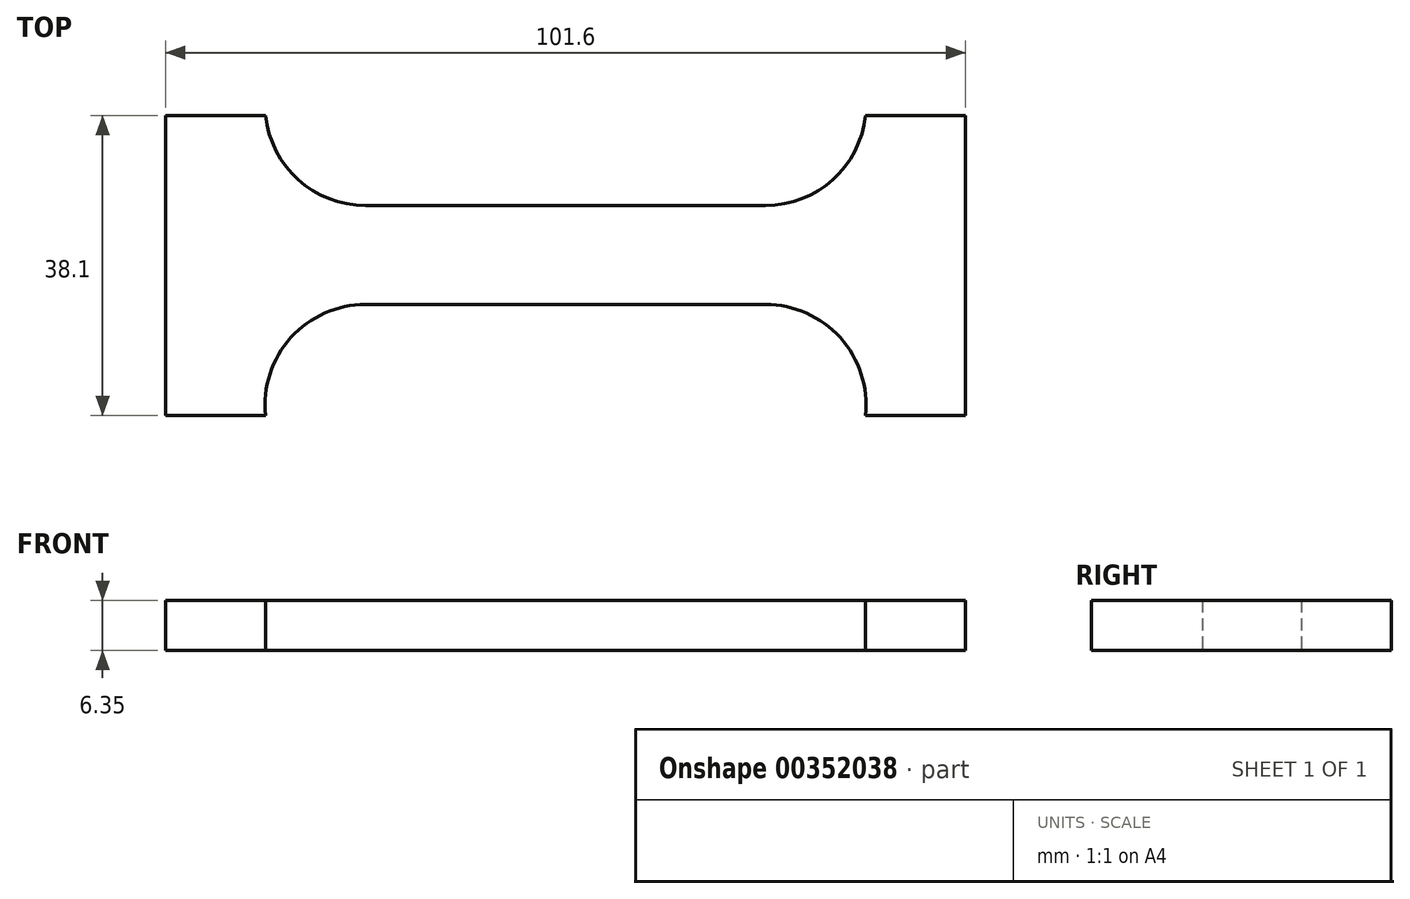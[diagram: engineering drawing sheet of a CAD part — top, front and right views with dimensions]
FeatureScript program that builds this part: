
annotation { "Feature Type Name" : "Feature", "Feature Type Description" : "" }
export const myFeature = defineFeature(function(context is Context, id is Id, definition is map)
    precondition{}
    {
        {
            var Q0;
            Q0=qCreatedBy(makeId("Top.planeOp"),FACE);
            var sketch = newSketch(context, id + "F0", { "sketchPlane" : qUnion([Q0])});
            skLineSegment(sketch, "E0", {"start": v(0, 0) * mm, "end": v(0, 6.28) * mm});
            skLineSegment(sketch, "E1", {"start": v(0, 6.28) * mm, "end": v(25.4, 6.28) * mm});
            skLineSegment(sketch, "E2", {"start": v(38.1, 17.7) * mm, "end": v(50.8, 17.7) * mm});
            skLineSegment(sketch, "E3", {"start": v(50.8, 17.7) * mm, "end": v(50.8, -20.4) * mm});
            skLineSegment(sketch, "E4", {"start": v(50.8, -20.4) * mm, "end": v(38.1, -20.4) * mm});
            skLineSegment(sketch, "E5", {"start": v(25.4, -6.28) * mm, "end": v(0, -6.28) * mm});
            skLineSegment(sketch, "E6", {"start": v(0, -6.28) * mm, "end": v(0, 0) * mm});
            skArc(sketch, "E7", {"start": v(25.4, 6.28) * mm, "mid": v(33.94, 9.56) * mm, "end": v(38.1, 17.7) * mm});
            skArc(sketch, "E8", {"start": v(25.4, -6.28) * mm, "mid": v(34.9, -10.5) * mm, "end": v(38.1, -20.4) * mm});
            skLineSegment(sketch, "E9.MirrorCS", {"start": v(-50.8, -20.4) * mm, "end": v(-38.1, -20.4) * mm});
            skLineSegment(sketch, "E10.MirrorCS", {"start": v(-50.8, 17.7) * mm, "end": v(-50.8, -20.4) * mm});
            skLineSegment(sketch, "E11.MirrorCS", {"start": v(-38.1, 17.7) * mm, "end": v(-50.8, 17.7) * mm});
            skLineSegment(sketch, "E12.MirrorCS", {"start": v(0, 6.28) * mm, "end": v(-25.4, 6.28) * mm});
            skArc(sketch, "E13.MirrorCS", {"start": v(-25.4, -6.28) * mm, "mid": v(-34.9, -10.5) * mm, "end": v(-38.1, -20.4) * mm});
            skArc(sketch, "E14.MirrorCS", {"start": v(-25.4, 6.28) * mm, "mid": v(-33.94, 9.56) * mm, "end": v(-38.1, 17.7) * mm});
            skLineSegment(sketch, "E15.MirrorCS", {"start": v(-25.4, -6.28) * mm, "end": v(0, -6.28) * mm});
            skSolve(sketch);
        }
        {
            var Q0;
            Q0=makeQuery(id+"F0.imprint","IMPRINT",FACE,{"disambiguationData":[TD([[makeQuery(id+"F0.imprint","IMPRINT",EDGE,{"derivedFrom":sQuery(id+"F0.wireOp",EDGE,"E6")}),1.0]])]});
            var Q1;
            Q1=makeQuery(id+"F0.imprint","IMPRINT",FACE,{"disambiguationData":[TD([[makeQuery(id+"F0.imprint","IMPRINT",EDGE,{"derivedFrom":sQuery(id+"F0.wireOp",EDGE,"E1")}),-1.0]])]});
            extrude(context, id + "F1", {"entities" : qUnion([Q0, Q1]), "depth" : 6.35 * mm});
        }
    });
